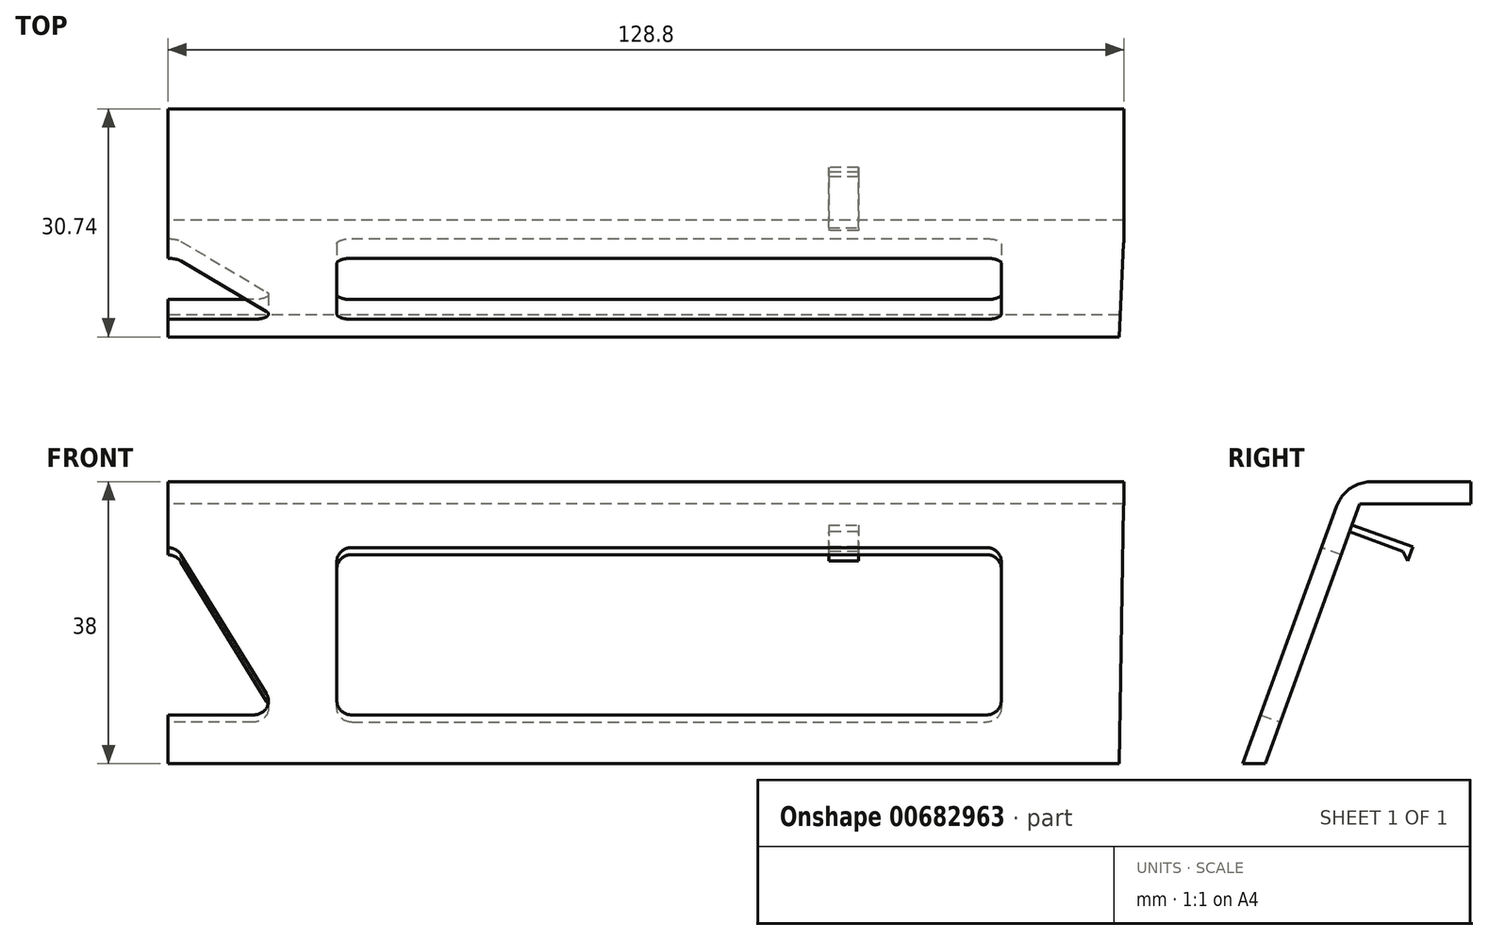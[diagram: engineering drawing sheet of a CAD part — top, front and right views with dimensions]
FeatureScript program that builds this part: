
annotation { "Feature Type Name" : "Feature", "Feature Type Description" : "" }
export const myFeature = defineFeature(function(context is Context, id is Id, definition is map)
    precondition{}
    {
        {
            var Q0;
            Q0=qCreatedBy(makeId("Right.planeOp"),FACE);
            var sketch = newSketch(context, id + "F0", { "sketchPlane" : qUnion([Q0])});
            skLineSegment(sketch, "E0", {"start": v(0, 0) * mm, "end": v(12.63, 34.71) * mm});
            skLineSegment(sketch, "E1", {"start": v(17.33, 38) * mm, "end": v(30.74, 38) * mm});
            skLineSegment(sketch, "E2", {"start": v(30.74, 38) * mm, "end": v(30.74, 35) * mm});
            skLineSegment(sketch, "E3", {"start": v(30.74, 35) * mm, "end": v(15.74, 35) * mm});
            skLineSegment(sketch, "E4", {"start": v(15.74, 35) * mm, "end": v(3, 0) * mm});
            skLineSegment(sketch, "E5", {"start": v(3, 0) * mm, "end": v(0, 0) * mm});
            skPoint(sketch, "E6.visualSharp", {"position": v(13.83, 38) * mm});
            skArc(sketch, "E6.filletArc", {"start": v(17.33, 38) * mm, "mid": v(14.46, 37.1) * mm, "end": v(12.63, 34.71) * mm});
            skSolve(sketch);
        }
        {
            var Q0;
            Q0=makeQuery(id+"F0.imprint","IMPRINT",FACE,{"disambiguationData":[TD([[makeQuery(id+"F0.imprint","IMPRINT",EDGE,{"derivedFrom":sQuery(id+"F0.wireOp",EDGE,"E1")}),-1.0]])]});
            extrude(context, id + "F1", {"entities" : qUnion([Q0]), "depth" : 129 * mm, "offsetDistance" : 25 * mm});
        }
        {
            var Q0;
            Q0=makeQuery(id+"F1.opExtrude","SWEPT_FACE",FACE,{"disambiguationData":[OSD([sQuery(id+"F0.wireOp",EDGE,"E0")])]});
            var sketch = newSketch(context, id + "F2", { "sketchPlane" : qUnion([Q0])});
            skLineSegment(sketch, "E7.bottom", {"start": v(110.25, 7) * mm, "end": v(24.75, 7) * mm});
            skLineSegment(sketch, "E7.top", {"start": v(110.25, 31) * mm, "end": v(24.75, 31) * mm});
            skLineSegment(sketch, "E7.left", {"start": v(112.25, 9) * mm, "end": v(112.25, 29) * mm});
            skLineSegment(sketch, "E7.right", {"start": v(22.75, 9) * mm, "end": v(22.75, 29) * mm});
            skPoint(sketch, "E8.visualSharp", {"position": v(112.25, 31) * mm});
            skArc(sketch, "E8.filletArc", {"start": v(112.25, 29) * mm, "mid": v(111.66, 30.41) * mm, "end": v(110.25, 31) * mm});
            skPoint(sketch, "E9.visualSharp", {"position": v(22.75, 31) * mm});
            skArc(sketch, "E9.filletArc", {"start": v(24.75, 31) * mm, "mid": v(23.34, 30.41) * mm, "end": v(22.75, 29) * mm});
            skPoint(sketch, "E10.visualSharp", {"position": v(22.75, 7) * mm});
            skArc(sketch, "E10.filletArc", {"start": v(22.75, 9) * mm, "mid": v(23.34, 7.59) * mm, "end": v(24.75, 7) * mm});
            skPoint(sketch, "E11.visualSharp", {"position": v(112.25, 7) * mm});
            skArc(sketch, "E11.filletArc", {"start": v(110.25, 7) * mm, "mid": v(111.66, 7.59) * mm, "end": v(112.25, 9) * mm});
            skLineSegment(sketch, "E12", {"start": v(-11.54, 7) * mm, "end": v(11.54, 7) * mm});
            skLineSegment(sketch, "E13", {"start": v(13.27, 10) * mm, "end": v(1.73, 29.98) * mm});
            skLineSegment(sketch, "E14", {"start": v(-1.73, 29.98) * mm, "end": v(-13.27, 10) * mm});
            skPoint(sketch, "E15.visualSharp", {"position": v(-15, 7) * mm});
            skArc(sketch, "E15.filletArc", {"start": v(-13.27, 10) * mm, "mid": v(-13.27, 8) * mm, "end": v(-11.54, 7) * mm});
            skPoint(sketch, "E16.visualSharp", {"position": v(15, 7) * mm});
            skArc(sketch, "E16.filletArc", {"start": v(11.54, 7) * mm, "mid": v(13.27, 8) * mm, "end": v(13.27, 10) * mm});
            skPoint(sketch, "E17.visualSharp", {"position": v(0, 32.98) * mm});
            skArc(sketch, "E17.filletArc", {"start": v(1.73, 29.98) * mm, "mid": v(0, 30.98) * mm, "end": v(-1.73, 29.98) * mm});
            skSolve(sketch);
        }
        {
            var Q0;
            Q0=makeQuery(id+"F2.imprint","IMPRINT",FACE,{"disambiguationData":[TD([[makeQuery(id+"F2.imprint","IMPRINT",EDGE,{"derivedFrom":sQuery(id+"F2.wireOp",EDGE,"E7.bottom")}),-1.0]])]});
            var Q1;
            Q1=makeQuery(id+"F2.imprint","IMPRINT",FACE,{"disambiguationData":[TD([[makeQuery(id+"F2.imprint","IMPRINT",EDGE,{"derivedFrom":sQuery(id+"F2.wireOp",EDGE,"E12")}),1.0]])]});
            extrude(context, id + "F3", {"entities" : qUnion([Q0, Q1]), "operationType" : NewBodyOperationType.REMOVE, "oppositeDirection" : true, "depth" : 25 * mm, "offsetDistance" : 25 * mm});
        }
        {
            var Q0;
            Q0=qCreatedBy(makeId("Front.planeOp"),FACE);
            var sketch = newSketch(context, id + "F4", { "sketchPlane" : qUnion([Q0])});
            skLineSegment(sketch, "E18", {"start": v(129, 50) * mm, "end": v(149, 50) * mm});
            skLineSegment(sketch, "E19", {"start": v(149, 50) * mm, "end": v(149, -10) * mm});
            skLineSegment(sketch, "E20", {"start": v(149, -10) * mm, "end": v(128, -10) * mm});
            skLineSegment(sketch, "E21", {"start": v(128, -10) * mm, "end": v(129, 50) * mm});
            skSolve(sketch);
        }
        {
            var Q0;
            Q0=makeQuery(id+"F4.imprint","IMPRINT",FACE,{"disambiguationData":[TD([[makeQuery(id+"F4.imprint","IMPRINT",EDGE,{"derivedFrom":sQuery(id+"F4.wireOp",EDGE,"E18")}),-1.0]])]});
            extrude(context, id + "F5", {"entities" : qUnion([Q0]), "operationType" : NewBodyOperationType.REMOVE, "oppositeDirection" : true, "depth" : 40 * mm, "offsetDistance" : 25 * mm});
        }
        {
            var Q0;
            Q0=qCreatedBy(makeId("Right.planeOp"),FACE);
            cPlane(context, id + "F6", {"entities" : qUnion([Q0]), "cplaneType" : CPlaneType.OFFSET, "offset" : 89 * mm, "width" : 150 * mm, "height" : 150 * mm});
        }
        {
            var Q0;
            Q0=qCreatedBy(id+"F6.planeOp",FACE);
            var sketch = newSketch(context, id + "F7", { "sketchPlane" : qUnion([Q0])});
            skLineSegment(sketch, "E22", {"start": v(13.47, 32.63) * mm, "end": v(22.87, 29.21) * mm});
            skLineSegment(sketch, "E23", {"start": v(22.87, 29.21) * mm, "end": v(22.19, 27.33) * mm});
            skLineSegment(sketch, "E24", {"start": v(22.19, 27.33) * mm, "end": v(21.59, 28.61) * mm});
            skLineSegment(sketch, "E25", {"start": v(21.59, 28.61) * mm, "end": v(13.13, 31.7) * mm});
            skLineSegment(sketch, "E26", {"start": v(13.13, 31.7) * mm, "end": v(13.47, 32.63) * mm});
            skSolve(sketch);
        }
        {
            var Q0;
            Q0=makeQuery(id+"F7.imprint","IMPRINT",FACE,{"disambiguationData":[TD([[makeQuery(id+"F7.imprint","IMPRINT",EDGE,{"derivedFrom":sQuery(id+"F7.wireOp",EDGE,"Z1IW9EHz-zkqJ-5XB8-BsIh-Ff4xYnMpoWtQ.bottom")}),-1.0]])]});
            var Q1;
            {var subQ0=sQuery(id+"F7.wireOp",EDGE,"d8hvF1dN-k6TA-Gqnt-z4S7-jDni1HmhoUw6");Q1=makeQuery(id+"F7.imprint","IMPRINT",FACE,{"disambiguationData":[TD([[makeQuery(id+"F7.imprint","IMPRINT",EDGE,{"derivedFrom":subQ0}),-1.0]])]});}
            var Q2;
            Q2=makeQuery(id+"F7.imprint","IMPRINT",FACE,{"disambiguationData":[TD([[makeQuery(id+"F7.imprint","IMPRINT",EDGE,{"derivedFrom":sQuery(id+"F7.wireOp",EDGE,"E22")}),-1.0]])]});
            extrude(context, id + "F8", {"entities" : qUnion([Q0, Q1, Q2]), "operationType" : NewBodyOperationType.ADD, "depth" : 4 * mm, "offsetDistance" : 25 * mm});
        }
    });
